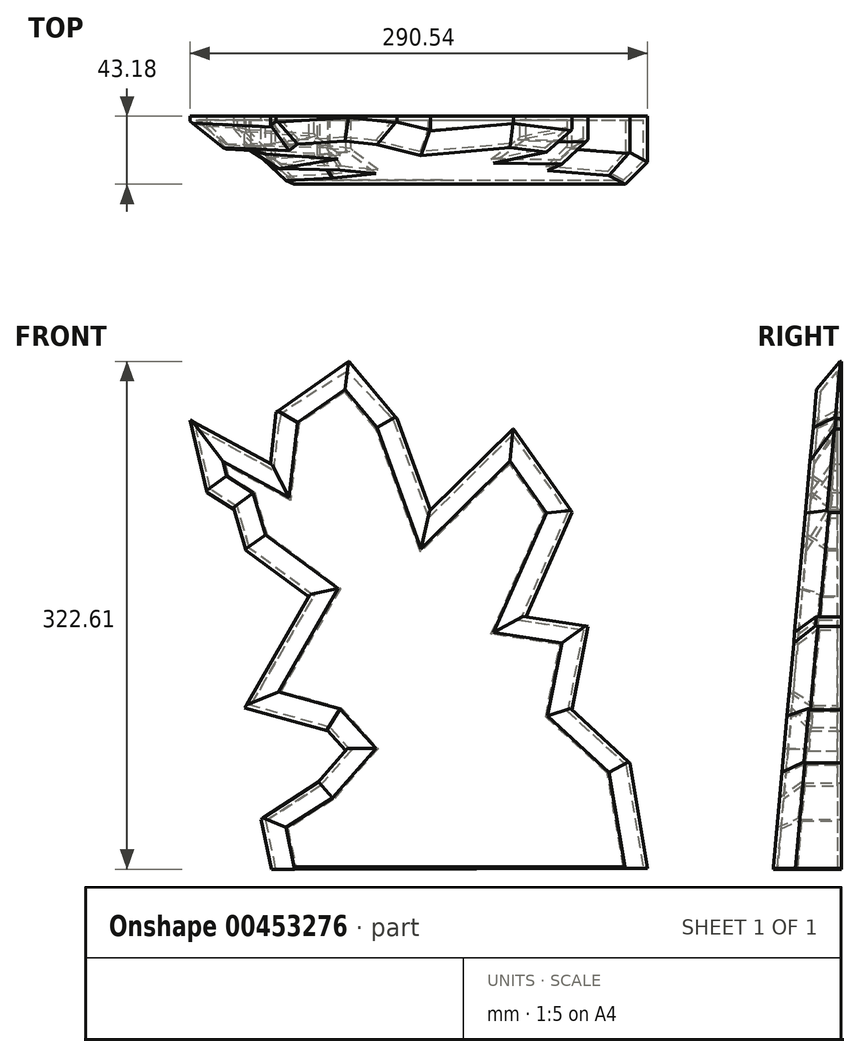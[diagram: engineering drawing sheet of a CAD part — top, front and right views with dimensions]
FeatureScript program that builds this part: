
annotation { "Feature Type Name" : "Feature", "Feature Type Description" : "" }
export const myFeature = defineFeature(function(context is Context, id is Id, definition is map)
    precondition{}
    {
        {
            var Q0;
            Q0=qCreatedBy(makeId("Front.planeOp"),FACE);
            var sketch = newSketch(context, id + "F0", { "sketchPlane" : qUnion([Q0])});
            skLineSegment(sketch, "E0", {"start": v(178.03, -22.3) * mm, "end": v(143.21, -44.73) * mm});
            skLineSegment(sketch, "E1", {"start": v(143.21, -44.73) * mm, "end": v(149.63, -75.31) * mm});
            skLineSegment(sketch, "E2", {"start": v(178.03, -22.3) * mm, "end": v(197.7, 0) * mm});
            skLineSegment(sketch, "E3", {"start": v(197.7, 0) * mm, "end": v(184.22, 14.85) * mm});
            skLineSegment(sketch, "E4", {"start": v(184.22, 14.85) * mm, "end": v(133.93, 28.77) * mm});
            skLineSegment(sketch, "E5", {"start": v(133.93, 28.77) * mm, "end": v(174.16, 98.41) * mm});
            skLineSegment(sketch, "E6", {"start": v(174.16, 98.41) * mm, "end": v(133.15, 128.59) * mm});
            skLineSegment(sketch, "E7", {"start": v(133.15, 128.59) * mm, "end": v(125.42, 154.9) * mm});
            skLineSegment(sketch, "E8", {"start": v(125.42, 154.9) * mm, "end": v(108.4, 165.73) * mm});
            skLineSegment(sketch, "E9", {"start": v(108.4, 165.73) * mm, "end": v(99.1, 205.19) * mm});
            skLineSegment(sketch, "E10", {"start": v(99.1, 205.19) * mm, "end": v(148.63, 178.1) * mm});
            skLineSegment(sketch, "E11", {"start": v(148.63, 178.1) * mm, "end": v(152.5, 213.7) * mm});
            skLineSegment(sketch, "E12", {"start": v(152.5, 213.7) * mm, "end": v(195.83, 243.88) * mm});
            skLineSegment(sketch, "E13", {"start": v(195.83, 243.88) * mm, "end": v(224.46, 209.83) * mm});
            skLineSegment(sketch, "E14", {"start": v(224.46, 209.83) * mm, "end": v(246.9, 147.93) * mm});
            skLineSegment(sketch, "E15", {"start": v(246.9, 147.93) * mm, "end": v(300.28, 200.55) * mm});
            skLineSegment(sketch, "E16", {"start": v(300.28, 200.55) * mm, "end": v(335.1, 151.03) * mm});
            skLineSegment(sketch, "E17", {"start": v(335.1, 151.03) * mm, "end": v(304.93, 82.94) * mm});
            skLineSegment(sketch, "E18", {"start": v(304.93, 82.94) * mm, "end": v(345.16, 76.75) * mm});
            skLineSegment(sketch, "E19", {"start": v(345.16, 76.75) * mm, "end": v(335.1, 24.9) * mm});
            skLineSegment(sketch, "E20", {"start": v(335.1, 24.9) * mm, "end": v(372.24, -9.14) * mm});
            skLineSegment(sketch, "E21", {"start": v(372.24, -9.14) * mm, "end": v(383.3, -74.7) * mm});
            skLineSegment(sketch, "E22", {"start": v(149.63, -75.31) * mm, "end": v(383.3, -74.7) * mm});
            skSolve(sketch);
        }
        {
            var Q0;
            Q0=makeQuery(id+"F0.imprint","IMPRINT",FACE,{"disambiguationData":[TD([[makeQuery(id+"F0.imprint","IMPRINT",EDGE,{"derivedFrom":sQuery(id+"F0.wireOp",EDGE,"4jVaLz0e-jmkg-CxpW-WCZx-YQ6AkGQFnCnR")}),-1.0]])]});
            var Q1;
            Q1=makeQuery(id+"F0.imprint","IMPRINT",FACE,{"disambiguationData":[TD([[makeQuery(id+"F0.imprint","IMPRINT",EDGE,{"derivedFrom":sQuery(id+"F0.wireOp",EDGE,"E0")}),1.0]])]});
            extrude(context, id + "F1", {"entities" : qUnion([Q0, Q1]), "depth" : 38.1 * mm, "offsetDistance" : 25.4 * mm});
        }
        {
            var Q0;
            Q0=qCreatedBy(makeId("Right.planeOp"),FACE);
            cPlane(context, id + "F2", {"entities" : qUnion([Q0]), "cplaneType" : CPlaneType.OFFSET, "offset" : 76.2 * mm, "oppositeDirection" : true, "width" : 152.4 * mm, "height" : 152.4 * mm});
        }
        {
            var Q0;
            Q0=qCreatedBy(id+"F2.planeOp",FACE);
            var sketch = newSketch(context, id + "F3", { "sketchPlane" : qUnion([Q0])});
            skLineSegment(sketch, "E23", {"start": v(-38.2, -75.6) * mm, "end": v(0, 347.56) * mm});
            skLineSegment(sketch, "E24", {"start": v(0, 347.56) * mm, "end": v(-59.26, 352.9) * mm});
            skLineSegment(sketch, "E25", {"start": v(-59.26, 352.9) * mm, "end": v(-38.2, -75.6) * mm});
            skSolve(sketch);
        }
        {
            var Q0;
            Q0=qSketchRegion(id+"F3",true);
            extrude(context, id + "F4", {"entities" : qUnion([Q0]), "operationType" : NewBodyOperationType.REMOVE, "endBound" : BoundingType.THROUGH_ALL, "depth" : 25.4 * mm});
        }
        {
            var Q0;
            Q0=makeQuery(id+"F4.boolean.opBoolean","COPY",FACE,{"derivedFrom":makeQuery(id+"F4.opExtrude","SWEPT_FACE",FACE,{"disambiguationData":[OSD([sQuery(id+"F3.wireOp",EDGE,"E23")])]})});
            chamfer(context, id + "F5", {"entities" : qUnion([Q0]), "width" : 12.7 * mm, "tangentPropagation" : true});
        }
        {
            var Q0;
            Q0=makeQuery(id+"F1.opExtrude","SWEPT_FACE",FACE,{"disambiguationData":[OSD([sQuery(id+"F0.wireOp",EDGE,"E22")])]});
            shell(context, id + "F6", {"entities" : qUnion([Q0]), "thickness" : 2.54 * mm, "oppositeDirection" : true});
        }
    });
